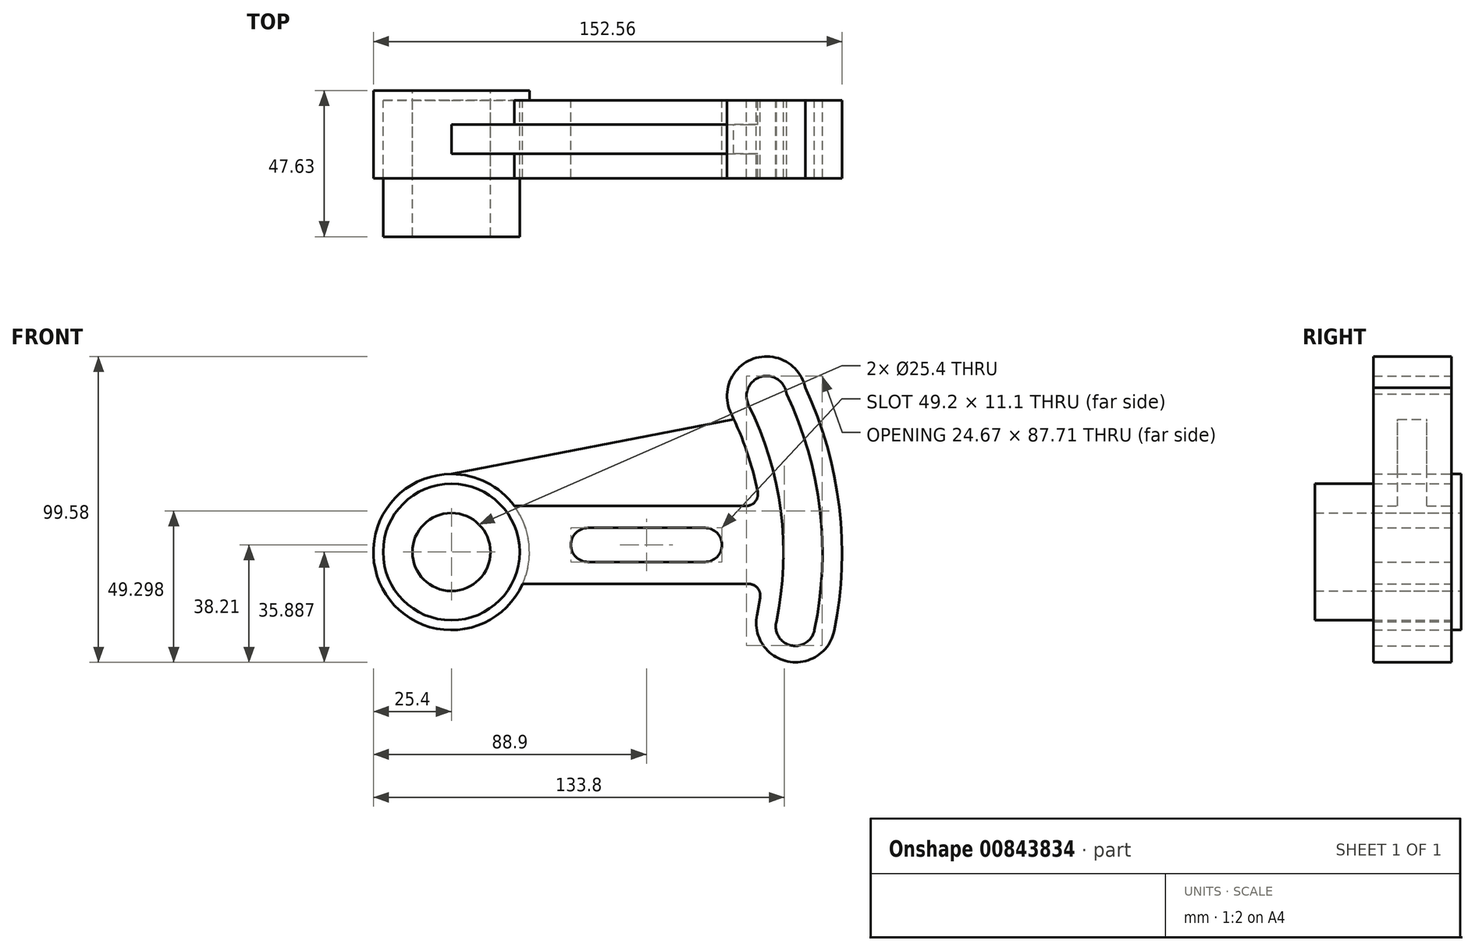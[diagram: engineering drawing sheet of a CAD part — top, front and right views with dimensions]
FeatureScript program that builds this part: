
annotation { "Feature Type Name" : "Feature", "Feature Type Description" : "" }
export const myFeature = defineFeature(function(context is Context, id is Id, definition is map)
    precondition{}
    {
        {
            var Q0;
            Q0=qCreatedBy(makeId("Front.planeOp"),FACE);
            var sketch = newSketch(context, id + "F0", { "sketchPlane" : qUnion([Q0])});
            skLineSegment(sketch, "E0.bottom", {"start": v(-43.02, 12.7) * mm, "end": v(28.67, 12.7) * mm});
            skLineSegment(sketch, "E0.top", {"start": v(-40.32, -12.7) * mm, "end": v(28.67, -12.7) * mm});
            skLineSegment(sketch, "E1.bottom", {"start": v(19.05, 5.55) * mm, "end": v(-19.05, 5.55) * mm});
            skLineSegment(sketch, "E1.top", {"start": v(19.05, -5.55) * mm, "end": v(-19.05, -5.55) * mm});
            skPoint(sketch, "E1.middle", {"position": v(0, 0) * mm});
            skPoint(sketch, "E2.third.point.positionSnap0", {"position": v(19.05, 0) * mm});
            skArc(sketch, "E3", {"start": v(-19.05, 5.55) * mm, "mid": v(-24.6, 0) * mm, "end": v(-19.05, -5.55) * mm});
            skArc(sketch, "E4", {"start": v(19.05, -5.55) * mm, "mid": v(24.6, 0) * mm, "end": v(19.05, 5.55) * mm});
            skCircle(sketch, "E5", {"center": v(-63.5, -2.32) * mm, "radius": 25.4 * mm});
            skPoint(sketch, "E5.third.point", {"position": v(-88.8, 0) * mm});
            skCircle(sketch, "E6", {"center": v(-63.5, -2.32) * mm, "radius": 12.7 * mm});
            skArc(sketch, "E7", {"start": v(36.01, -22.82) * mm, "mid": v(36.56, -19.95) * mm, "end": v(37.03, -17.06) * mm});
            skLineSegment(sketch, "E8", {"start": v(28.67, 12.7) * mm, "end": v(32.46, 12.7) * mm});
            skLineSegment(sketch, "E9", {"start": v(28.67, -12.7) * mm, "end": v(33.26, -12.7) * mm});
            skArc(sketch, "E10.trimOffspring", {"start": v(36.2, 17.24) * mm, "mid": v(32.72, 30.29) * mm, "end": v(27.55, 42.76) * mm});
            skArc(sketch, "E11.filletArc", {"start": v(37.03, -17.06) * mm, "mid": v(36.14, -14.02) * mm, "end": v(33.26, -12.7) * mm});
            skArc(sketch, "E12.filletArc", {"start": v(32.46, 12.7) * mm, "mid": v(35.4, 14.09) * mm, "end": v(36.2, 17.24) * mm});
            skCircle(sketch, "E13", {"center": v(-63.5, -2.32) * mm, "radius": 22.23 * mm});
            skArc(sketch, "E14.0", {"start": v(54.7, -27.66) * mm, "mid": v(56.48, 11.52) * mm, "end": v(45.6, 49.2) * mm});
            skArc(sketch, "E15.0", {"start": v(42.19, -25.4) * mm, "mid": v(43.77, 10.84) * mm, "end": v(33.25, 45.56) * mm});
            skArc(sketch, "E16", {"start": v(45.6, 49.2) * mm, "mid": v(37.25, 54.75) * mm, "end": v(33.25, 45.56) * mm});
            skArc(sketch, "E17.0", {"start": v(61.12, -27.95) * mm, "mid": v(62.78, 12.34) * mm, "end": v(51.71, 51.13) * mm});
            skArc(sketch, "E18", {"start": v(51.71, 51.13) * mm, "mid": v(34.88, 60.66) * mm, "end": v(27.55, 42.76) * mm});
            skLineSegment(sketch, "E19", {"start": v(-63.5, -2.32) * mm, "end": v(-63.5, 23.08) * mm, "construction": true});
            skLineSegment(sketch, "E20", {"start": v(-63.5, 23.08) * mm, "end": v(34.87, 23.08) * mm, "construction": true});
            skLineSegment(sketch, "E21", {"start": v(-63.5, 23.08) * mm, "end": v(28.43, 40.95) * mm});
            skLineSegment(sketch, "E22", {"start": v(19.05, 0) * mm, "end": v(19.05, -25.4) * mm, "construction": true});
            skArc(sketch, "E23", {"start": v(36.01, -22.82) * mm, "mid": v(46, -37.95) * mm, "end": v(61.12, -27.95) * mm});
            skLineSegment(sketch, "E24", {"start": v(42.19, -25.4) * mm, "end": v(54.7, -27.66) * mm, "construction": true});
            skPoint(sketch, "E25", {"position": v(48.44, -26.53) * mm});
            skArc(sketch, "E26", {"start": v(42.27, -25) * mm, "mid": v(47.11, -32.74) * mm, "end": v(54.7, -27.66) * mm});
            skSolve(sketch);
        }
        {
            var Q0;
            {var subQ1=sQuery(id+"F0.wireOp",EDGE,"E0.bottom");Q0=makeQuery(id+"F0.imprint","IMPRINT",FACE,{"disambiguationData":[TD([[makeQuery(id+"F0.imprint","IMPRINT",EDGE,{"derivedFrom":subQ1}),-1.0]])]});}
            var Q1;
            Q1=makeQuery(id+"F0.imprint","IMPRINT",FACE,{"disambiguationData":[TD([[makeQuery(id+"F0.imprint","IMPRINT",EDGE,{"derivedFrom":sQuery(id+"F0.wireOp",EDGE,"E13")}),-1.0]])]});
            var Q2;
            Q2=makeQuery(id+"F0.imprint","IMPRINT",FACE,{"disambiguationData":[TD([[makeQuery(id+"F0.imprint","IMPRINT",EDGE,{"derivedFrom":sQuery(id+"F0.wireOp",EDGE,"E6")}),-1.0]])]});
            extrude(context, id + "F1", {"entities" : qUnion([Q0, Q1, Q2]), "depth" : 25.4 * mm, "offsetDistance" : 25.4 * mm});
        }
        {
            var Q0;
            Q0=makeQuery(id+"F0.imprint","IMPRINT",FACE,{"disambiguationData":[TD([[makeQuery(id+"F0.imprint","IMPRINT",EDGE,{"derivedFrom":sQuery(id+"F0.wireOp",EDGE,"E6")}),-1.0]])]});
            extrude(context, id + "F2", {"entities" : qUnion([Q0]), "depth" : 44.45 * mm, "offsetDistance" : 25.4 * mm});
        }
        {
            var Q0;
            Q0=makeQuery(id+"F0.imprint","IMPRINT",FACE,{"disambiguationData":[TD([[makeQuery(id+"F0.imprint","IMPRINT",EDGE,{"derivedFrom":sQuery(id+"F0.wireOp",EDGE,"E6")}),-1.0]])]});
            var Q1;
            Q1=makeQuery(id+"F0.imprint","IMPRINT",FACE,{"disambiguationData":[TD([[makeQuery(id+"F0.imprint","IMPRINT",EDGE,{"derivedFrom":sQuery(id+"F0.wireOp",EDGE,"E13")}),-1.0]])]});
            extrude(context, id + "F3", {"entities" : qUnion([Q0, Q1]), "oppositeDirection" : true, "depth" : 3.17 * mm, "offsetDistance" : 25.4 * mm});
        }
        {
            var Q0;
            {var subQ3=sQuery(id+"F0.wireOp",EDGE,"E0.bottom");Q0=makeQuery(id+"F0.imprint","IMPRINT",FACE,{"disambiguationData":[TD([[makeQuery(id+"F0.imprint","IMPRINT",EDGE,{"derivedFrom":subQ3}),1.0]])]});}
            extrude(context, id + "F4", {"entities" : qUnion([Q0]), "operationType" : NewBodyOperationType.ADD, "depth" : 17.45 * mm, "offsetDistance" : 25.4 * mm});
        }
        {
            var Q0;
            {var subQ3=sQuery(id+"F0.wireOp",EDGE,"E0.bottom");Q0=makeQuery(id+"F0.imprint","IMPRINT",FACE,{"disambiguationData":[TD([[makeQuery(id+"F0.imprint","IMPRINT",EDGE,{"derivedFrom":subQ3}),1.0]])]});}
            extrude(context, id + "F5", {"entities" : qUnion([Q0]), "operationType" : NewBodyOperationType.REMOVE, "depth" : 7.92 * mm, "offsetDistance" : 25.4 * mm});
        }
    });
